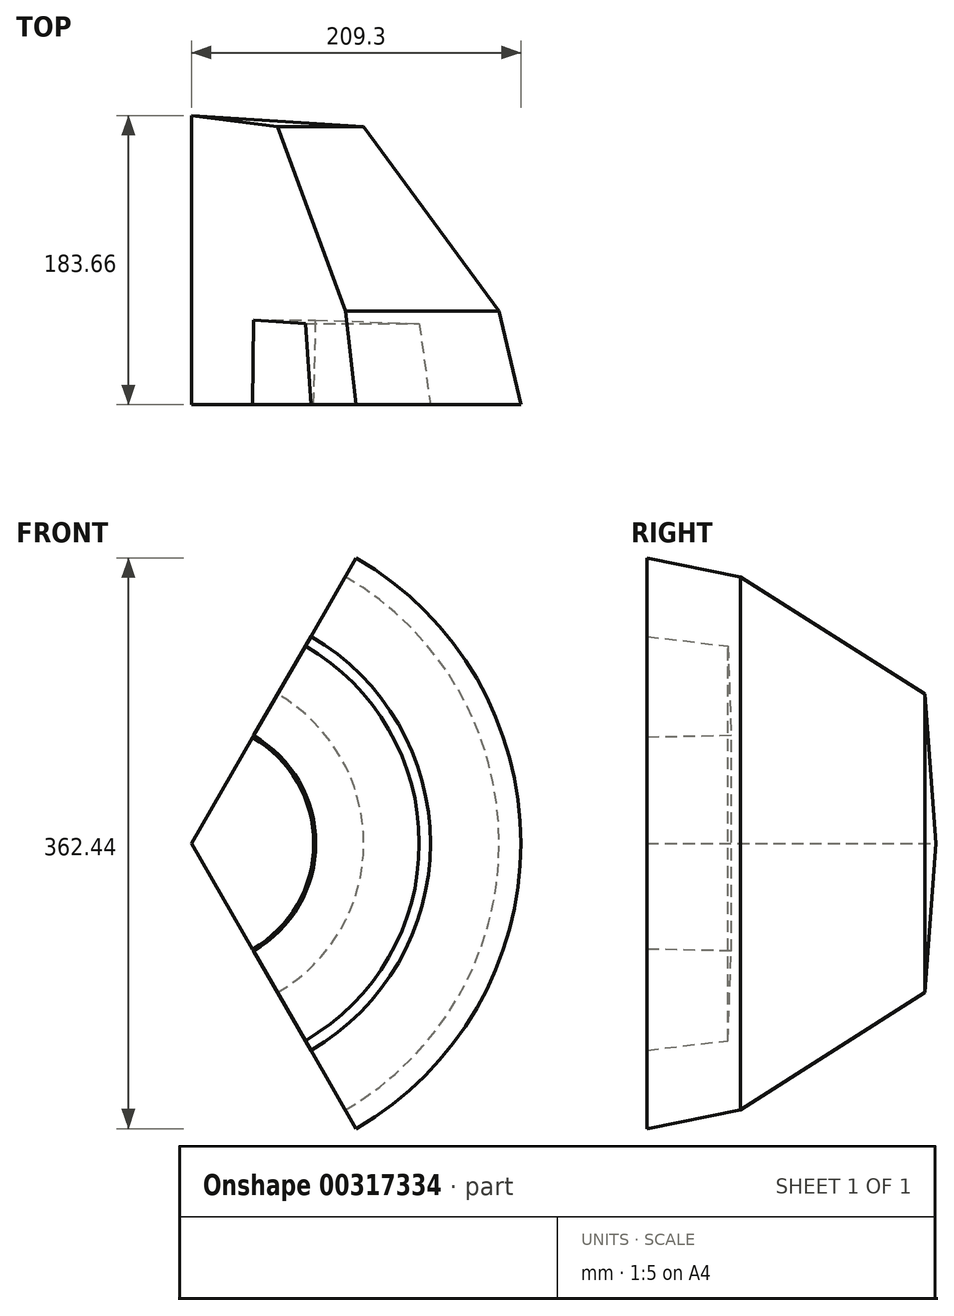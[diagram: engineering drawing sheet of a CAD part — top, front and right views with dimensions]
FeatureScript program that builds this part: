
annotation { "Feature Type Name" : "Feature", "Feature Type Description" : "" }
export const myFeature = defineFeature(function(context is Context, id is Id, definition is map)
    precondition{}
    {
        {
            var Q0;
            Q0=qCreatedBy(makeId("Top.planeOp"),FACE);
            var sketch = newSketch(context, id + "F0", { "sketchPlane" : qUnion([Q0])});
            skLineSegment(sketch, "E0", {"start": v(0, 0) * mm, "end": v(0, 183.66) * mm});
            skLineSegment(sketch, "E1", {"start": v(0, 183.66) * mm, "end": v(109.45, 176.65) * mm});
            skLineSegment(sketch, "E2", {"start": v(109.45, 176.65) * mm, "end": v(195.52, 59.45) * mm});
            skLineSegment(sketch, "E3", {"start": v(195.52, 59.45) * mm, "end": v(209.3, 0) * mm});
            skLineSegment(sketch, "E4", {"start": v(209.3, 0) * mm, "end": v(151.8, 0) * mm});
            skLineSegment(sketch, "E5", {"start": v(151.8, 0) * mm, "end": v(144.72, 51.41) * mm});
            skLineSegment(sketch, "E6", {"start": v(144.72, 51.41) * mm, "end": v(78.97, 53.65) * mm});
            skLineSegment(sketch, "E7", {"start": v(78.97, 53.65) * mm, "end": v(77.7, 0) * mm});
            skLineSegment(sketch, "E8", {"start": v(77.7, 0) * mm, "end": v(0, 0) * mm});
            skSolve(sketch);
        }
        {
            var Q0;
            Q0=makeQuery(id+"F0.imprint","IMPRINT",FACE,{"disambiguationData":[TD([[makeQuery(id+"F0.imprint","IMPRINT",EDGE,{"derivedFrom":sQuery(id+"F0.wireOp",EDGE,"E0")}),-1.0]])]});
            var Q1;
            Q1=sQuery(id+"F0.wireOp",EDGE,"E0");
            revolve(context, id + "F1", {"entities" : qUnion([Q0]), "axis" : qUnion([Q1]), "revolveType" : RevolveType.SYMMETRIC, "angle" : 119.96 * degree});
        }
    });
